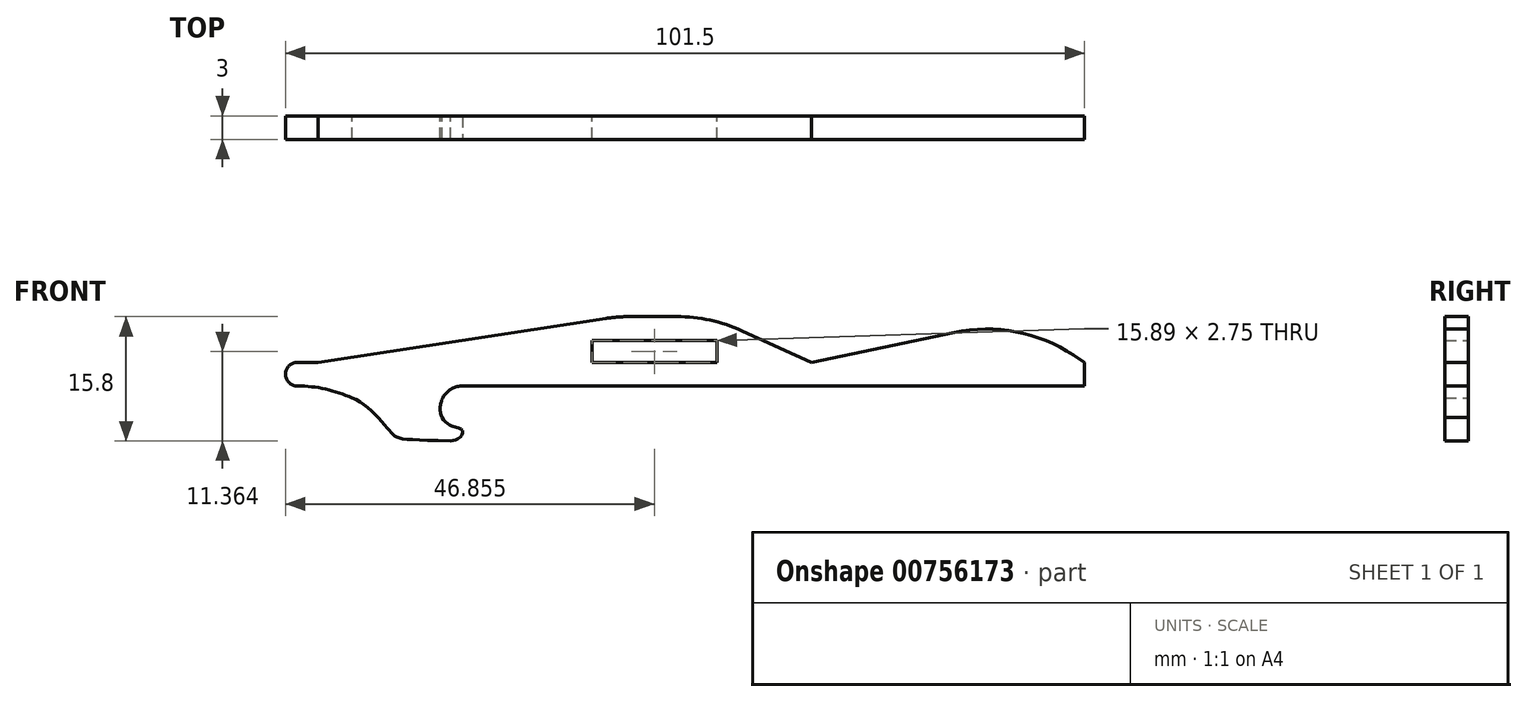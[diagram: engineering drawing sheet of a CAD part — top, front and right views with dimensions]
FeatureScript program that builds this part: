
annotation { "Feature Type Name" : "Feature", "Feature Type Description" : "" }
export const myFeature = defineFeature(function(context is Context, id is Id, definition is map)
    precondition{}
    {
        {
            var Q0;
            Q0=qCreatedBy(makeId("Front.planeOp"),FACE);
            var sketch = newSketch(context, id + "F0", { "sketchPlane" : qUnion([Q0])});
            skLineSegment(sketch, "E0.bottom", {"start": v(37.78, 37.08) * mm, "end": v(-62.22, 37.08) * mm});
            skLineSegment(sketch, "E0.top", {"start": v(37.78, 34.08) * mm, "end": v(-41.22, 34.08) * mm});
            skLineSegment(sketch, "E0.left", {"start": v(37.78, 37.08) * mm, "end": v(37.78, 34.08) * mm});
            skLineSegment(sketch, "E0.right", {"start": v(-62.22, 37.08) * mm, "end": v(-62.22, 34.08) * mm});
            skLineSegment(sketch, "E1.bottom", {"start": v(-62.22, 34.08) * mm, "end": v(-41.22, 34.08) * mm});
            skLineSegment(sketch, "E2.bottom", {"start": v(-54.06, 34.08) * mm, "end": v(-41.27, 34.08) * mm});
            skArc(sketch, "E3", {"start": v(-41.22, 34.08) * mm, "mid": v(-43.61, 32.78) * mm, "end": v(-43.84, 30.06) * mm});
            skArc(sketch, "E4", {"start": v(-55.25, 32.55) * mm, "mid": v(-58.65, 33.7) * mm, "end": v(-62.22, 34.08) * mm});
            skFitSpline(sketch, "E5", {"points": [v(-42.78, 27.1) * mm, v(-50.6, 28.5) * mm, v(-55.25, 32.55) * mm], "startDerivative": vector(-39.18, 1.2) * mm, "endDerivative": vector(-11.06, 3.92) * mm});
            skFitSpline(sketch, "E6", {"points": [v(-43.84, 30.06) * mm, v(-41.27, 28.45) * mm, v(-42.78, 27.1) * mm], "startDerivative": vector(4.8, -7.71) * mm, "endDerivative": vector(-8.49, -0.39) * mm});
            skLineSegment(sketch, "E7.left", {"start": v(-24.81, 39.83) * mm, "end": v(-24.81, 37.08) * mm});
            skLineSegment(sketch, "E7.right", {"start": v(-8.92, 39.83) * mm, "end": v(-8.92, 37.08) * mm});
            skLineSegment(sketch, "E8", {"start": v(-24.81, 39.83) * mm, "end": v(-8.92, 39.83) * mm});
            skLineSegment(sketch, "E9", {"start": v(-59.6, 37.08) * mm, "end": v(-23, 42.67) * mm});
            skLineSegment(sketch, "E10", {"start": v(-19.98, 42.9) * mm, "end": v(-14.03, 42.9) * mm});
            skLineSegment(sketch, "E11", {"start": v(-5.74, 41.1) * mm, "end": v(3.08, 37.08) * mm});
            skLineSegment(sketch, "E12", {"start": v(3.08, 37.08) * mm, "end": v(21.25, 40.89) * mm});
            skLineSegment(sketch, "E13", {"start": v(36.35, 38.02) * mm, "end": v(37.78, 37.08) * mm});
            skLineSegment(sketch, "E14", {"start": v(-24.81, 37.08) * mm, "end": v(-8.92, 37.08) * mm});
            skPoint(sketch, "E15.visualSharp", {"position": v(-9.7, 42.9) * mm});
            skArc(sketch, "E15.filletArc", {"start": v(-5.74, 41.1) * mm, "mid": v(-9.79, 42.44) * mm, "end": v(-14.03, 42.9) * mm});
            skPoint(sketch, "E16.visualSharp", {"position": v(-21.5, 42.9) * mm});
            skArc(sketch, "E16.filletArc", {"start": v(-19.98, 42.9) * mm, "mid": v(-21.5, 42.84) * mm, "end": v(-23, 42.67) * mm});
            skPoint(sketch, "E17.visualSharp", {"position": v(29.4, 42.6) * mm});
            skArc(sketch, "E17.filletArc", {"start": v(36.35, 38.02) * mm, "mid": v(29.09, 40.96) * mm, "end": v(21.25, 40.89) * mm});
            skArc(sketch, "E18", {"start": v(-62.22, 37.08) * mm, "mid": v(-63.72, 35.58) * mm, "end": v(-62.22, 34.08) * mm});
            skLineSegment(sketch, "E19", {"start": v(21.25, 40.89) * mm, "end": v(40.76, 52.65) * mm});
            skLineSegment(sketch, "E20", {"start": v(44.84, 48.53) * mm, "end": v(37.78, 37.08) * mm});
            skPoint(sketch, "E21.visualSharp", {"position": v(51.28, 58.99) * mm});
            skArc(sketch, "E21.filletArc", {"start": v(44.84, 48.53) * mm, "mid": v(44.42, 52.2) * mm, "end": v(40.76, 52.65) * mm});
            skSolve(sketch);
        }
        {
            var Q0;
            Q0=makeQuery(id+"F0.imprint","IMPRINT",FACE,{"disambiguationData":[TD([[makeQuery(id+"F0.imprint","IMPRINT",EDGE,{"derivedFrom":sQuery(id+"F0.wireOp",EDGE,"E0.right")}),-1.0]])]});
            var Q1;
            {var subQ0=sQuery(id+"F0.wireOp",EDGE,"E3");Q1=makeQuery(id+"F0.imprint","IMPRINT",FACE,{"disambiguationData":[TD([[makeQuery(id+"F0.imprint","IMPRINT",EDGE,{"derivedFrom":subQ0}),-1.0]])]});}
            var Q2;
            {var subQ3=sQuery(id+"F0.wireOp",EDGE,"E7.left");Q2=makeQuery(id+"F0.imprint","IMPRINT",FACE,{"disambiguationData":[TD([[makeQuery(id+"F0.imprint","IMPRINT",EDGE,{"derivedFrom":subQ3}),-1.0]])]});}
            var Q3;
            {var subQ6=sQuery(id+"F0.wireOp",EDGE,"E0.top");Q3=makeQuery(id+"F0.imprint","IMPRINT",FACE,{"disambiguationData":[TD([[makeQuery(id+"F0.imprint","IMPRINT",EDGE,{"derivedFrom":subQ6}),-1.0]])]});}
            var Q4;
            {var subQ2=sQuery(id+"F0.wireOp",EDGE,"E12");Q4=makeQuery(id+"F0.imprint","IMPRINT",FACE,{"disambiguationData":[TD([[makeQuery(id+"F0.imprint","IMPRINT",EDGE,{"derivedFrom":subQ2}),-1.0]])]});}
            extrude(context, id + "F1", {"entities" : qUnion([Q0, Q1, Q2, Q3, Q4]), "depth" : 3 * mm, "offsetDistance" : 25 * mm});
        }
    });
